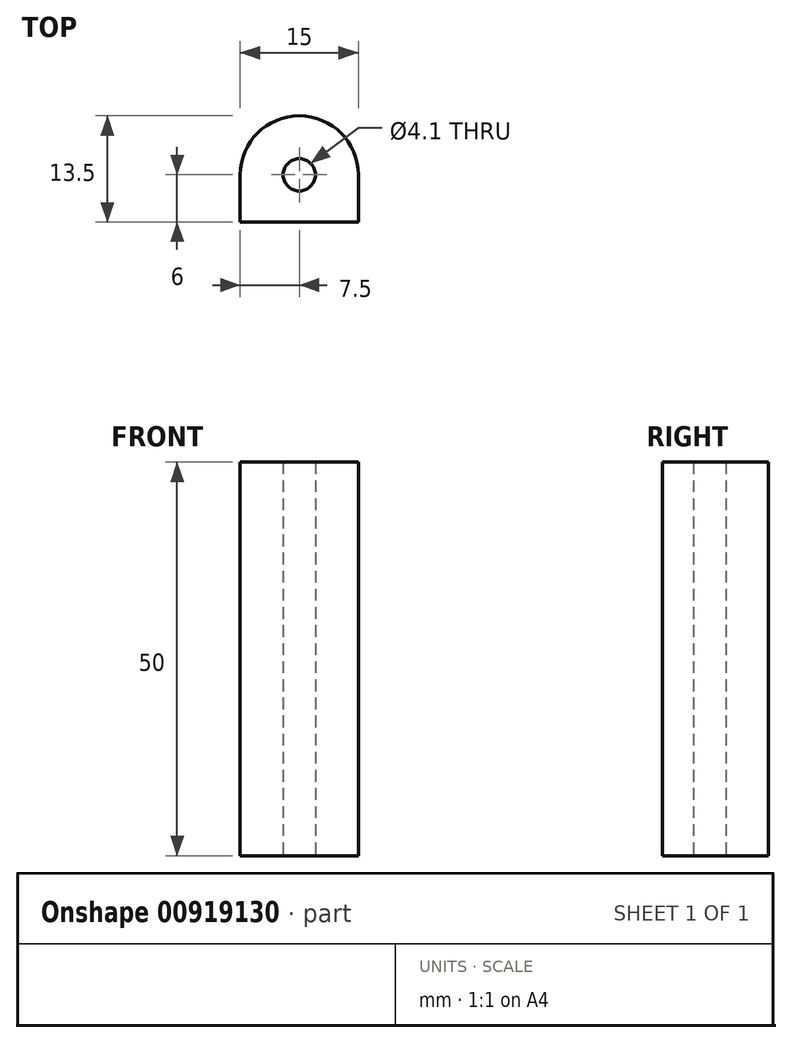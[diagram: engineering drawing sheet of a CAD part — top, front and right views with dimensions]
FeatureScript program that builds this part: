
annotation { "Feature Type Name" : "Feature", "Feature Type Description" : "" }
export const myFeature = defineFeature(function(context is Context, id is Id, definition is map)
    precondition{}
    {
        {
            var Q0;
            Q0=qCreatedBy(makeId("Top.planeOp"),FACE);
            var sketch = newSketch(context, id + "F0", { "sketchPlane" : qUnion([Q0])});
            skCircle(sketch, "E0", {"center": v(0, 0) * mm, "radius": 2.05 * mm});
            skArc(sketch, "E1", {"start": v(-7.5, 0) * mm, "mid": v(0, 7.5) * mm, "end": v(7.5, 0) * mm});
            skLineSegment(sketch, "E2", {"start": v(-7.5, 0) * mm, "end": v(-7.5, -6) * mm});
            skLineSegment(sketch, "E3", {"start": v(-7.5, -6) * mm, "end": v(7.5, -6) * mm});
            skLineSegment(sketch, "E4", {"start": v(7.5, -6) * mm, "end": v(7.5, 0) * mm});
            skLineSegment(sketch, "E5", {"start": v(0, -6) * mm, "end": v(0, 0) * mm, "construction": true});
            skSolve(sketch);
        }
        {
            var Q0;
            Q0=makeQuery(id+"F0.imprint","IMPRINT",FACE,{"disambiguationData":[TD([[makeQuery(id+"F0.imprint","IMPRINT",EDGE,{"derivedFrom":sQuery(id+"F0.wireOp",EDGE,"E0")}),-1.0]])]});
            extrude(context, id + "F1", {"entities" : qUnion([Q0]), "depth" : 50 * mm, "offsetDistance" : 25 * mm});
        }
    });
